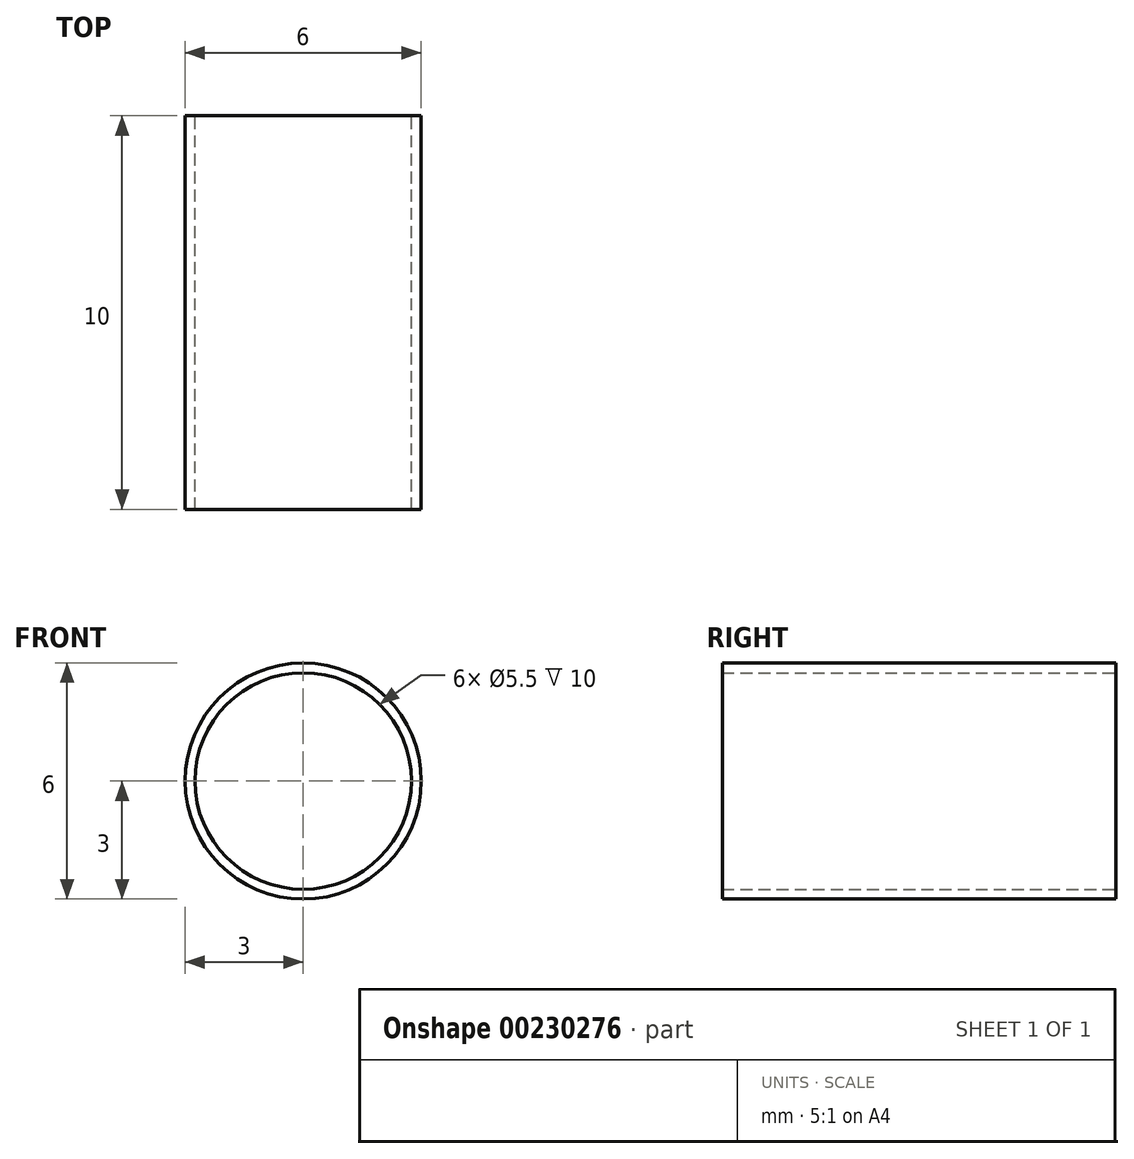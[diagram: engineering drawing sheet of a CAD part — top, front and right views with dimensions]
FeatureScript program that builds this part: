
annotation { "Feature Type Name" : "Feature", "Feature Type Description" : "" }
export const myFeature = defineFeature(function(context is Context, id is Id, definition is map)
    precondition{}
    {
        {
            var Q0;
            Q0=qCreatedBy(makeId("Front.planeOp"),FACE);
            var sketch = newSketch(context, id + "F0", { "sketchPlane" : qUnion([Q0])});
            skCircle(sketch, "E0", {"center": v(0, 0) * mm, "radius": 3 * mm});
            skCircle(sketch, "E1", {"center": v(0, 0) * mm, "radius": 2.75 * mm});
            skSolve(sketch);
        }
        {
            var Q0;
            Q0=makeQuery(id+"F0.imprint","IMPRINT",FACE,{"disambiguationData":[TD([[makeQuery(id+"F0.imprint","IMPRINT",EDGE,{"derivedFrom":sQuery(id+"F0.wireOp",EDGE,"E0")}),1.0]])]});
            extrude(context, id + "F1", {"entities" : qUnion([Q0]), "endBound" : BoundingType.SYMMETRIC, "depth" : 10 * mm});
        }
    });
